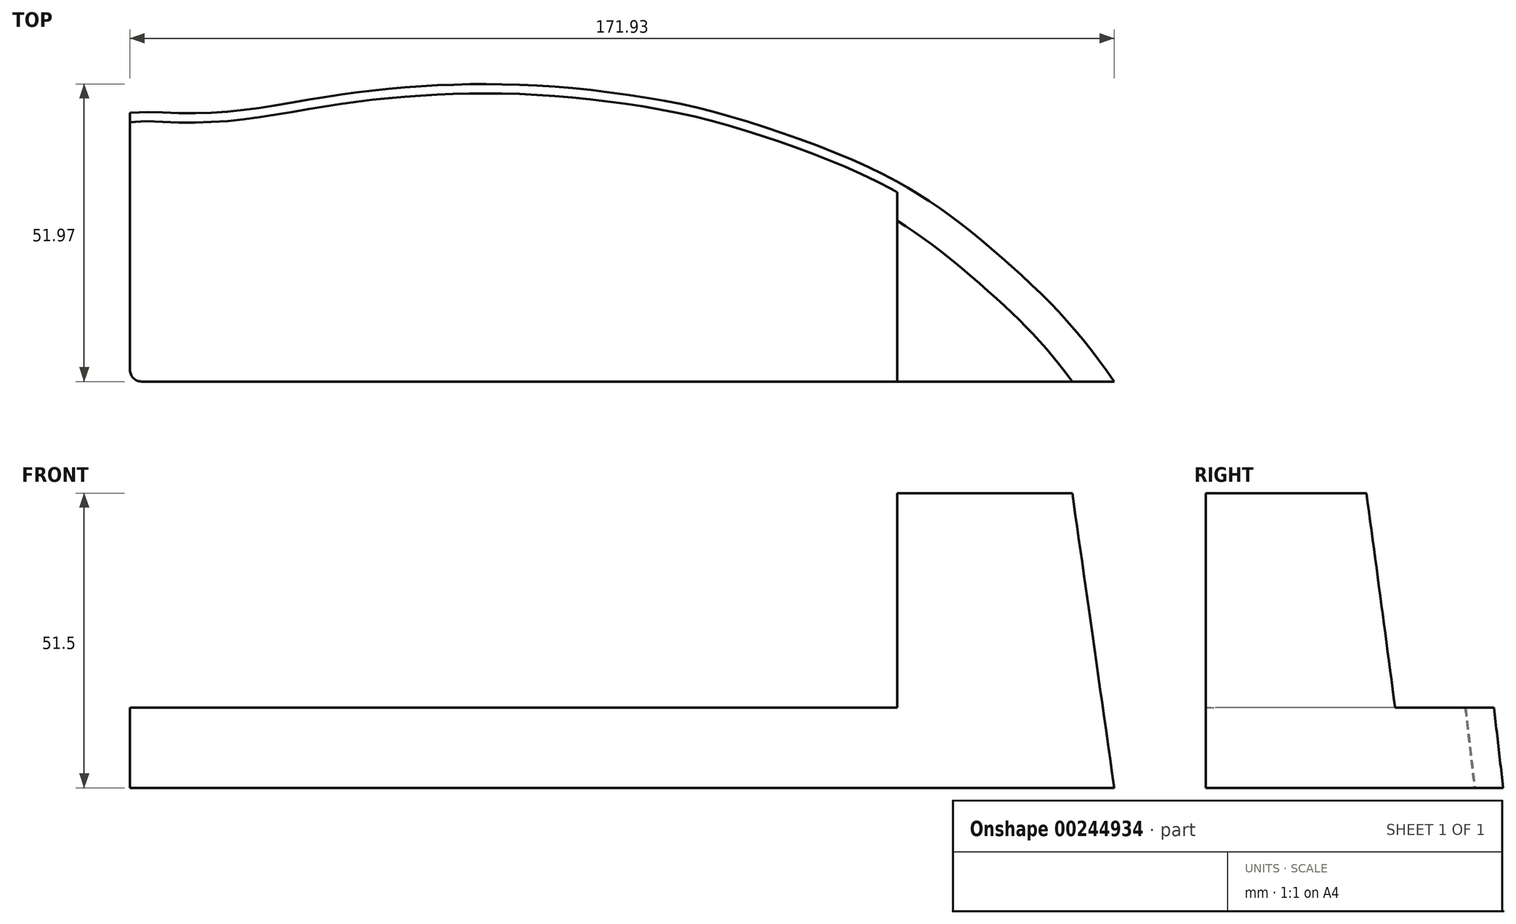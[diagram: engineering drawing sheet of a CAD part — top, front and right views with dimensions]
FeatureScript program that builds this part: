
annotation { "Feature Type Name" : "Feature", "Feature Type Description" : "" }
export const myFeature = defineFeature(function(context is Context, id is Id, definition is map)
    precondition{}
    {
        {
            var Q0;
            Q0=qCreatedBy(makeId("Top.planeOp"),FACE);
            var sketch = newSketch(context, id + "F0", { "sketchPlane" : qUnion([Q0])});
            skLineSegment(sketch, "E0", {"start": v(0, 0) * mm, "end": v(172, 0) * mm});
            skLineSegment(sketch, "E1", {"start": v(0, 0) * mm, "end": v(0, 47) * mm});
            skFitSpline(sketch, "E2", {"points": [v(0, 47) * mm, v(6.24, 47.01) * mm, v(17.54, 47.25) * mm, v(36.45, 50.14) * mm, v(65, 52) * mm, v(91.7, 49.41) * mm, v(108.42, 45.31) * mm, v(134, 35) * mm, v(150.7, 23.09) * mm, v(160.95, 13.63) * mm, v(172, 0) * mm], "startDerivative": vector(211.9, 12.85) * mm, "endDerivative": vector(135.28, -193.9) * mm});
            skLineSegment(sketch, "E3", {"start": v(0, 0) * mm, "end": v(65, 0) * mm});
            skLineSegment(sketch, "E4", {"start": v(65, 0) * mm, "end": v(65, 52) * mm});
            skLineSegment(sketch, "E5", {"start": v(172, 0) * mm, "end": v(134, 0) * mm});
            skLineSegment(sketch, "E6", {"start": v(134, 0) * mm, "end": v(134, 35) * mm});
            skSolve(sketch);
        }
        {
            var Q0;
            Q0 = qSketchRegion(id + "F0", true);
            extrude(context, id + "F1", {"entities" : qUnion([Q0]), "depth" : 51.5 * mm});
        }
        {
            var Q0;
            Q0=makeQuery(id+"F1.opExtrude","CAP_EDGE",EDGE,{"disambiguationData":[OSD([sQuery(id+"F0.wireOp",EDGE,"E2")])],"isStart":false});
            chamfer(context, id + "F2", {"entities" : qUnion([Q0]), "chamferType" : ChamferType.TWO_OFFSETS, "width1" : 52 * mm, "oppositeDirection" : false, "width2" : 6 * mm, "tangentPropagation" : true});
        }
        {
            var Q0;
            Q0=qCreatedBy(makeId("Front.planeOp"),FACE);
            var sketch = newSketch(context, id + "F3", { "sketchPlane" : qUnion([Q0])});
            skLineSegment(sketch, "E7", {"start": v(0, 0) * mm, "end": v(0, 14) * mm});
            skLineSegment(sketch, "E8.bottom", {"start": v(0, 14) * mm, "end": v(134, 14) * mm});
            skLineSegment(sketch, "E8.top", {"start": v(0, 58.88) * mm, "end": v(134, 58.88) * mm});
            skLineSegment(sketch, "E8.left", {"start": v(0, 14) * mm, "end": v(0, 58.88) * mm});
            skLineSegment(sketch, "E8.right", {"start": v(134, 14) * mm, "end": v(134, 58.88) * mm});
            skSolve(sketch);
        }
        {
            var Q0;
            Q0 = qSketchRegion(id + "F3", true);
            extrude(context, id + "F4", {"entities" : qUnion([Q0]), "operationType" : NewBodyOperationType.REMOVE, "oppositeDirection" : true, "depth" : 60 * mm});
        }
        {
            var Q0;
            Q0=makeQuery(id+"F2.opChamfer","BLEND_EDGE",EDGE,{"blendedFrom":[makeQuery(id+"F1.opExtrude","CAP_EDGE",EDGE,{"disambiguationData":[OSD([sQuery(id+"F0.wireOp",EDGE,"E2")])],"isStart":false}),makeQuery(id+"F1.opExtrude","SWEPT_FACE",FACE,{"disambiguationData":[OSD([sQuery(id+"F0.wireOp",EDGE,"E1")])]})],"blendedInto":[makeQuery(id+"F1.opExtrude","SWEPT_FACE",FACE,{"disambiguationData":[OSD([sQuery(id+"F0.wireOp",EDGE,"E1")])]})]});
            var Q1;
            Q1=makeQuery(id+"F1.opExtrude","SWEPT_EDGE",EDGE,{"disambiguationData":[OSD([sQuery(id+"F0.wireOp",EDGE,"E1"),sQuery(id+"F0.wireOp",EDGE,"E3")])]});
            fillet(context, id + "F5", {"entities" : qUnion([Q0, Q1]), "radius" : 2 * mm, "tangentPropagation" : true, "allowEdgeOverflow" : false});
        }
    });
